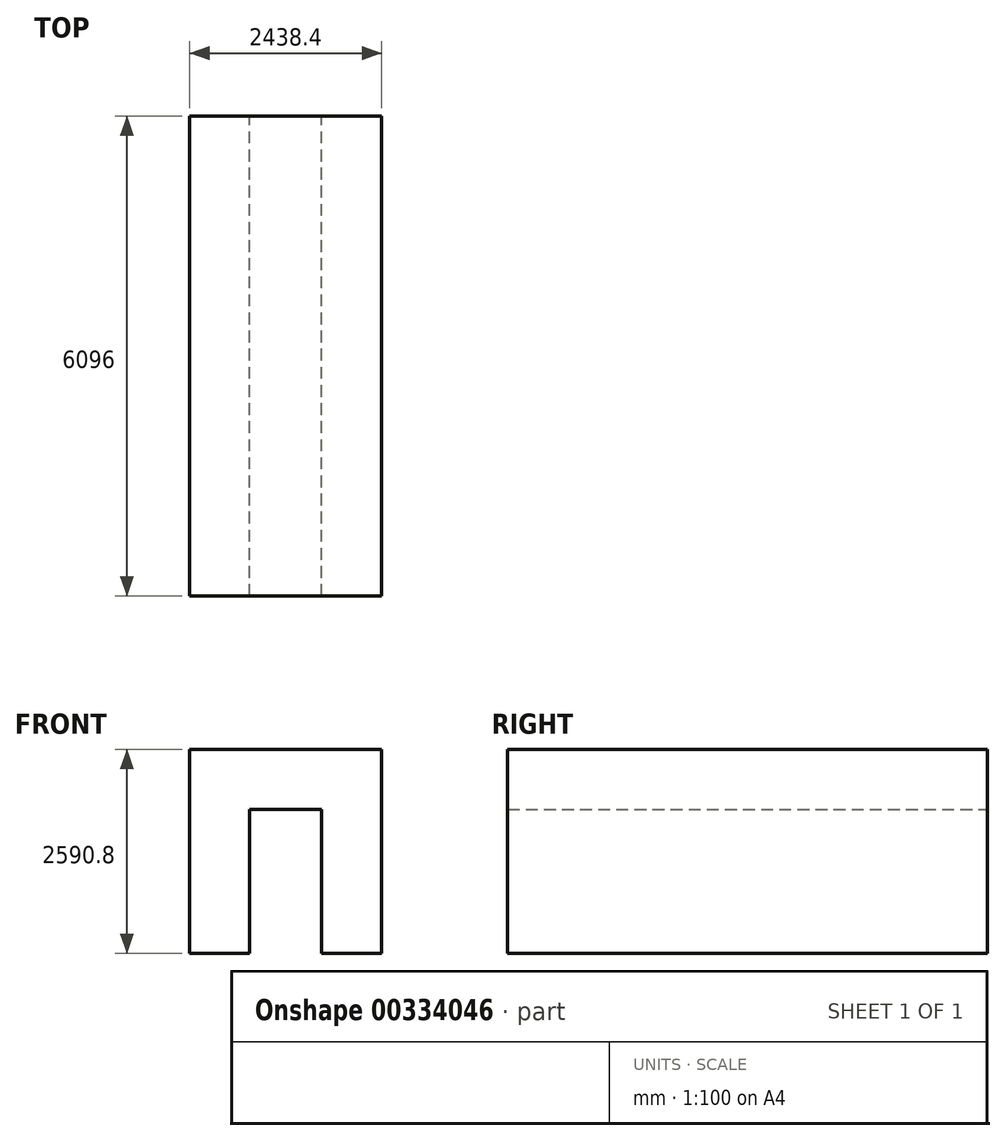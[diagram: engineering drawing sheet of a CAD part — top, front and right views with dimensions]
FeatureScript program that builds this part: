
annotation { "Feature Type Name" : "Feature", "Feature Type Description" : "" }
export const myFeature = defineFeature(function(context is Context, id is Id, definition is map)
    precondition{}
    {
        {
            var Q0;
            Q0=qCreatedBy(makeId("Front.planeOp"),FACE);
            var sketch = newSketch(context, id + "F0", { "sketchPlane" : qUnion([Q0])});
            skLineSegment(sketch, "E0.bottom", {"start": v(-1219.2, 1295.4) * mm, "end": v(1219.2, 1295.4) * mm});
            skLineSegment(sketch, "E0.top", {"start": v(-1219.2, -1295.4) * mm, "end": v(1219.2, -1295.4) * mm});
            skLineSegment(sketch, "E0.left", {"start": v(-1219.2, 1295.4) * mm, "end": v(-1219.2, -1295.4) * mm});
            skLineSegment(sketch, "E0.right", {"start": v(1219.2, 1295.4) * mm, "end": v(1219.2, -1295.4) * mm});
            skPoint(sketch, "E0.middle", {"position": v(0, 533.4) * mm});
            skLineSegment(sketch, "E1", {"start": v(0, 1295.4) * mm, "end": v(0, -1295.4) * mm, "construction": true});
            skLineSegment(sketch, "E2", {"start": v(0, 533.4) * mm, "end": v(-457.2, 533.4) * mm});
            skLineSegment(sketch, "E3", {"start": v(-457.2, 533.4) * mm, "end": v(-457.2, -1295.4) * mm});
            skLineSegment(sketch, "E4", {"start": v(-457.2, -1295.4) * mm, "end": v(454.85, -1295.4) * mm});
            skLineSegment(sketch, "E5.MirrorCS", {"start": v(0, 533.4) * mm, "end": v(457.2, 533.4) * mm});
            skLineSegment(sketch, "E6.MirrorCS", {"start": v(457.2, 533.4) * mm, "end": v(457.2, -1295.4) * mm});
            skSolve(sketch);
        }
        {
            var Q0;
            Q0 = qSketchRegion(id + "F0", true);
            extrude(context, id + "F1", {"entities" : qUnion([Q0]), "depth" : 6096 * mm});
        }
        {
            var Q0;
            Q0=makeQuery(id+"F0.imprint","IMPRINT",FACE,{"disambiguationData":[TD([[makeQuery(id+"F0.imprint","IMPRINT",EDGE,{"derivedFrom":sQuery(id+"F0.wireOp",EDGE,"E2")}),1.0]])]});
            extrude(context, id + "F2", {"entities" : qUnion([Q0]), "operationType" : NewBodyOperationType.REMOVE, "endBound" : BoundingType.THROUGH_ALL, "depth" : 6096 * mm});
        }
    });
